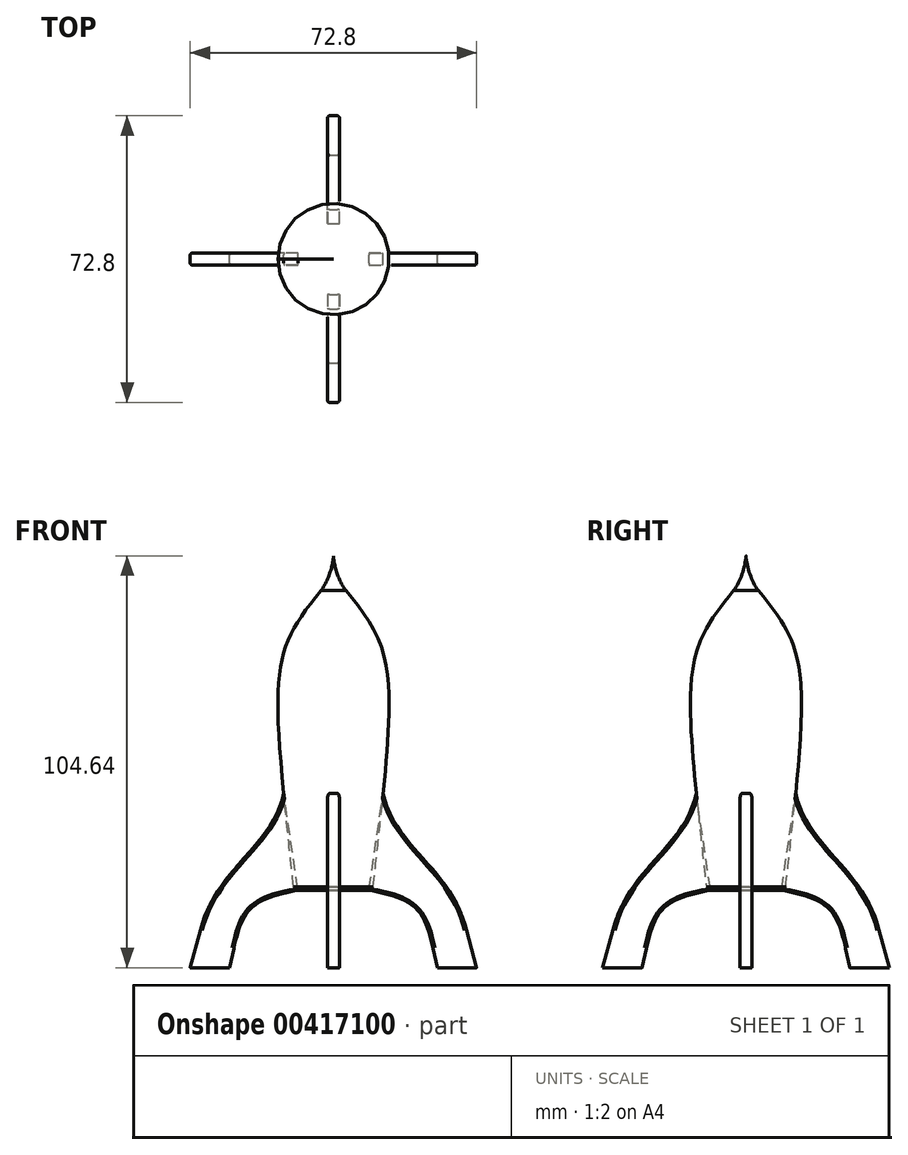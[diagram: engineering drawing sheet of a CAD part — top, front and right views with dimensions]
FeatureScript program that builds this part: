
annotation { "Feature Type Name" : "Feature", "Feature Type Description" : "" }
export const myFeature = defineFeature(function(context is Context, id is Id, definition is map)
    precondition{}
    {
        {
            var Q0;
            Q0=qCreatedBy(makeId("Front.planeOp"),FACE);
            var sketch = newSketch(context, id + "F0", { "sketchPlane" : qUnion([Q0])});
            skFitSpline(sketch, "E0", {"points": [v(-10, 0) * mm, v(0, 80) * mm], "startDerivative": vector(-19.84, 180) * mm, "endDerivative": vector(49.84, 60) * mm});
            skLineSegment(sketch, "E1", {"start": v(-10, 0) * mm, "end": v(0, 0) * mm});
            skLineSegment(sketch, "E2", {"start": v(0, 80) * mm, "end": v(0, 0) * mm});
            skFitSpline(sketch, "E3", {"points": [v(-3.18, 76.14) * mm, v(0, 85) * mm], "startDerivative": vector(5.65, 7) * mm, "endDerivative": vector(0, 6) * mm});
            skLineSegment(sketch, "E4", {"start": v(0, 85) * mm, "end": v(0, 80) * mm});
            skSolve(sketch);
        }
        {
            var Q0;
            Q0=makeQuery(id+"F0.imprint","IMPRINT",FACE,{"disambiguationData":[TD([[makeQuery(id+"F0.imprint","IMPRINT",EDGE,{"derivedFrom":sQuery(id+"F0.wireOp",EDGE,"E0")}),-1.0]])]});
            var Q1;
            {var subQ2=sQuery(id+"F0.wireOp",EDGE,"E3");Q1=makeQuery(id+"F0.imprint","IMPRINT",FACE,{"disambiguationData":[TD([[makeQuery(id+"F0.imprint","IMPRINT",EDGE,{"derivedFrom":subQ2}),-1.0]])]});}
            var Q2;
            Q2=sQuery(id+"F0.wireOp",EDGE,"E2");
            revolve(context, id + "F1", {"entities" : qUnion([Q0, Q1]), "axis" : qUnion([Q2]), "revolveType" : RevolveType.FULL});
        }
        {
            var Q0;
            Q0=qCreatedBy(makeId("Front.planeOp"),FACE);
            var sketch = newSketch(context, id + "F2", { "sketchPlane" : qUnion([Q0])});
            skFitSpline(sketch, "E5", {"points": [v(-9, 0) * mm, v(-25.31, -14.76) * mm], "startDerivative": vector(-36, -6) * mm, "endDerivative": vector(-6.51, -29.28) * mm});
            skLineSegment(sketch, "E6", {"start": v(-25.31, -14.76) * mm, "end": v(-26.4, -19.64) * mm});
            skLineSegment(sketch, "E7", {"start": v(-26.4, -19.64) * mm, "end": v(-36.4, -19.64) * mm});
            skLineSegment(sketch, "E8", {"start": v(-36.4, -19.64) * mm, "end": v(-33.8, -9.98) * mm});
            skFitSpline(sketch, "E9", {"points": [v(-33.8, -9.98) * mm, v(-12.64, 24.65) * mm], "startDerivative": vector(12.81, 47.81) * mm, "endDerivative": vector(8.7, 41.09) * mm});
            skLineSegment(sketch, "E10", {"start": v(-9, 0) * mm, "end": v(-12.64, 24.65) * mm});
            skLineSegment(sketch, "E11.MirrorCS", {"start": v(25.31, -14.76) * mm, "end": v(26.4, -19.64) * mm});
            skLineSegment(sketch, "E12.MirrorCS", {"start": v(26.4, -19.64) * mm, "end": v(36.4, -19.64) * mm});
            skFitSpline(sketch, "E13.MirrorCS", {"points": [v(9, 0) * mm, v(25.31, -14.76) * mm], "startDerivative": vector(36, -6) * mm, "endDerivative": vector(6.51, -29.28) * mm});
            skLineSegment(sketch, "E14.MirrorCS", {"start": v(9, 0) * mm, "end": v(12.64, 24.65) * mm});
            skLineSegment(sketch, "E15.MirrorCS", {"start": v(36.4, -19.64) * mm, "end": v(33.8, -9.98) * mm});
            skFitSpline(sketch, "E16.MirrorCS", {"points": [v(33.8, -9.98) * mm, v(12.64, 24.65) * mm], "startDerivative": vector(-12.81, 47.81) * mm, "endDerivative": vector(-8.7, 41.09) * mm});
            skSolve(sketch);
        }
        {
            var Q0;
            Q0=qSketchRegion(id+"F2",true);
            extrude(context, id + "F3", {"entities" : qUnion([Q0]), "endBound" : BoundingType.SYMMETRIC, "depth" : 3 * mm});
        }
        {
            var Q0;
            Q0=makeQuery(id+"F3.opExtrude","CAP_EDGE",EDGE,{"disambiguationData":[OSD([sQuery(id+"F2.wireOp",EDGE,"E16.MirrorCS")])],"isStart":true});
            var Q1;
            Q1=makeQuery(id+"F3.opExtrude","CAP_EDGE",EDGE,{"disambiguationData":[OSD([sQuery(id+"F2.wireOp",EDGE,"E15.MirrorCS")])],"isStart":true});
            var Q2;
            Q2=makeQuery(id+"F3.opExtrude","CAP_EDGE",EDGE,{"disambiguationData":[OSD([sQuery(id+"F2.wireOp",EDGE,"E13.MirrorCS")])],"isStart":true});
            var Q3;
            Q3=makeQuery(id+"F3.opExtrude","CAP_EDGE",EDGE,{"disambiguationData":[OSD([sQuery(id+"F2.wireOp",EDGE,"E11.MirrorCS")])],"isStart":true});
            var Q4;
            Q4=makeQuery(id+"F3.opExtrude","CAP_EDGE",EDGE,{"disambiguationData":[OSD([sQuery(id+"F2.wireOp",EDGE,"E15.MirrorCS")])],"isStart":false});
            var Q5;
            Q5=makeQuery(id+"F3.opExtrude","CAP_EDGE",EDGE,{"disambiguationData":[OSD([sQuery(id+"F2.wireOp",EDGE,"E16.MirrorCS")])],"isStart":false});
            var Q6;
            Q6=makeQuery(id+"F3.opExtrude","CAP_EDGE",EDGE,{"disambiguationData":[OSD([sQuery(id+"F2.wireOp",EDGE,"E13.MirrorCS")])],"isStart":false});
            var Q7;
            Q7=makeQuery(id+"F3.opExtrude","CAP_EDGE",EDGE,{"disambiguationData":[OSD([sQuery(id+"F2.wireOp",EDGE,"E11.MirrorCS")])],"isStart":false});
            var Q8;
            Q8=makeQuery(id+"F3.opExtrude","CAP_EDGE",EDGE,{"disambiguationData":[OSD([sQuery(id+"F2.wireOp",EDGE,"E6")])],"isStart":false});
            var Q9;
            Q9=makeQuery(id+"F3.opExtrude","CAP_EDGE",EDGE,{"disambiguationData":[OSD([sQuery(id+"F2.wireOp",EDGE,"E5")])],"isStart":false});
            var Q10;
            Q10=makeQuery(id+"F3.opExtrude","CAP_EDGE",EDGE,{"disambiguationData":[OSD([sQuery(id+"F2.wireOp",EDGE,"E5")])],"isStart":true});
            var Q11;
            Q11=makeQuery(id+"F3.opExtrude","CAP_EDGE",EDGE,{"disambiguationData":[OSD([sQuery(id+"F2.wireOp",EDGE,"E6")])],"isStart":true});
            var Q12;
            Q12=makeQuery(id+"F3.opExtrude","CAP_EDGE",EDGE,{"disambiguationData":[OSD([sQuery(id+"F2.wireOp",EDGE,"E8")])],"isStart":false});
            var Q13;
            Q13=makeQuery(id+"F3.opExtrude","CAP_EDGE",EDGE,{"disambiguationData":[OSD([sQuery(id+"F2.wireOp",EDGE,"E9")])],"isStart":false});
            var Q14;
            Q14=makeQuery(id+"F3.opExtrude","CAP_EDGE",EDGE,{"disambiguationData":[OSD([sQuery(id+"F2.wireOp",EDGE,"E8")])],"isStart":true});
            var Q15;
            Q15=makeQuery(id+"F3.opExtrude","CAP_EDGE",EDGE,{"disambiguationData":[OSD([sQuery(id+"F2.wireOp",EDGE,"E9")])],"isStart":true});
            fillet(context, id + "F4", {"entities" : qUnion([Q0, Q1, Q2, Q3, Q4, Q5, Q6, Q7, Q8, Q9, Q10, Q11, Q12, Q13, Q14, Q15]), "radius" : 0.5 * mm, "tangentPropagation" : true, "allowEdgeOverflow" : false});
        }
        {
            var Q0;
            Q0=makeQuery(id+"F3.opExtrude","SWEPT_BODY",BODY,{"disambiguationData":[OSD([sQuery(id+"F2.wireOp",EDGE,"E11.MirrorCS"),sQuery(id+"F2.wireOp",EDGE,"E12.MirrorCS"),sQuery(id+"F2.wireOp",EDGE,"E13.MirrorCS"),sQuery(id+"F2.wireOp",EDGE,"E14.MirrorCS"),sQuery(id+"F2.wireOp",EDGE,"E15.MirrorCS"),sQuery(id+"F2.wireOp",EDGE,"E16.MirrorCS")])]});
            var Q1;
            Q1=makeQuery(id+"F3.opExtrude","SWEPT_BODY",BODY,{"disambiguationData":[OSD([sQuery(id+"F2.wireOp",EDGE,"E5"),sQuery(id+"F2.wireOp",EDGE,"E6"),sQuery(id+"F2.wireOp",EDGE,"E7"),sQuery(id+"F2.wireOp",EDGE,"E8"),sQuery(id+"F2.wireOp",EDGE,"E9"),sQuery(id+"F2.wireOp",EDGE,"E10")])]});
            var Q2;
            Q2=sQuery(id+"F0.wireOp",EDGE,"E2");
            circularPattern(context, id + "F5", {"entities" : qUnion([Q0, Q1]), "axis" : qUnion([Q2]), "angle" : 90 * degree, "instanceCount" : 2, "equalSpace" : true});
        }
        {
            var Q0;
            Q0=makeQuery(id+"F1.opRevolve","SWEPT_EDGE",EDGE,{"disambiguationData":[OSD([sQuery(id+"F0.wireOp",EDGE,"E0"),sQuery(id+"F0.wireOp",EDGE,"E1")])]});
            fillet(context, id + "F6", {"entities" : qUnion([Q0]), "radius" : 1 * mm, "tangentPropagation" : true, "allowEdgeOverflow" : false});
        }
    });
